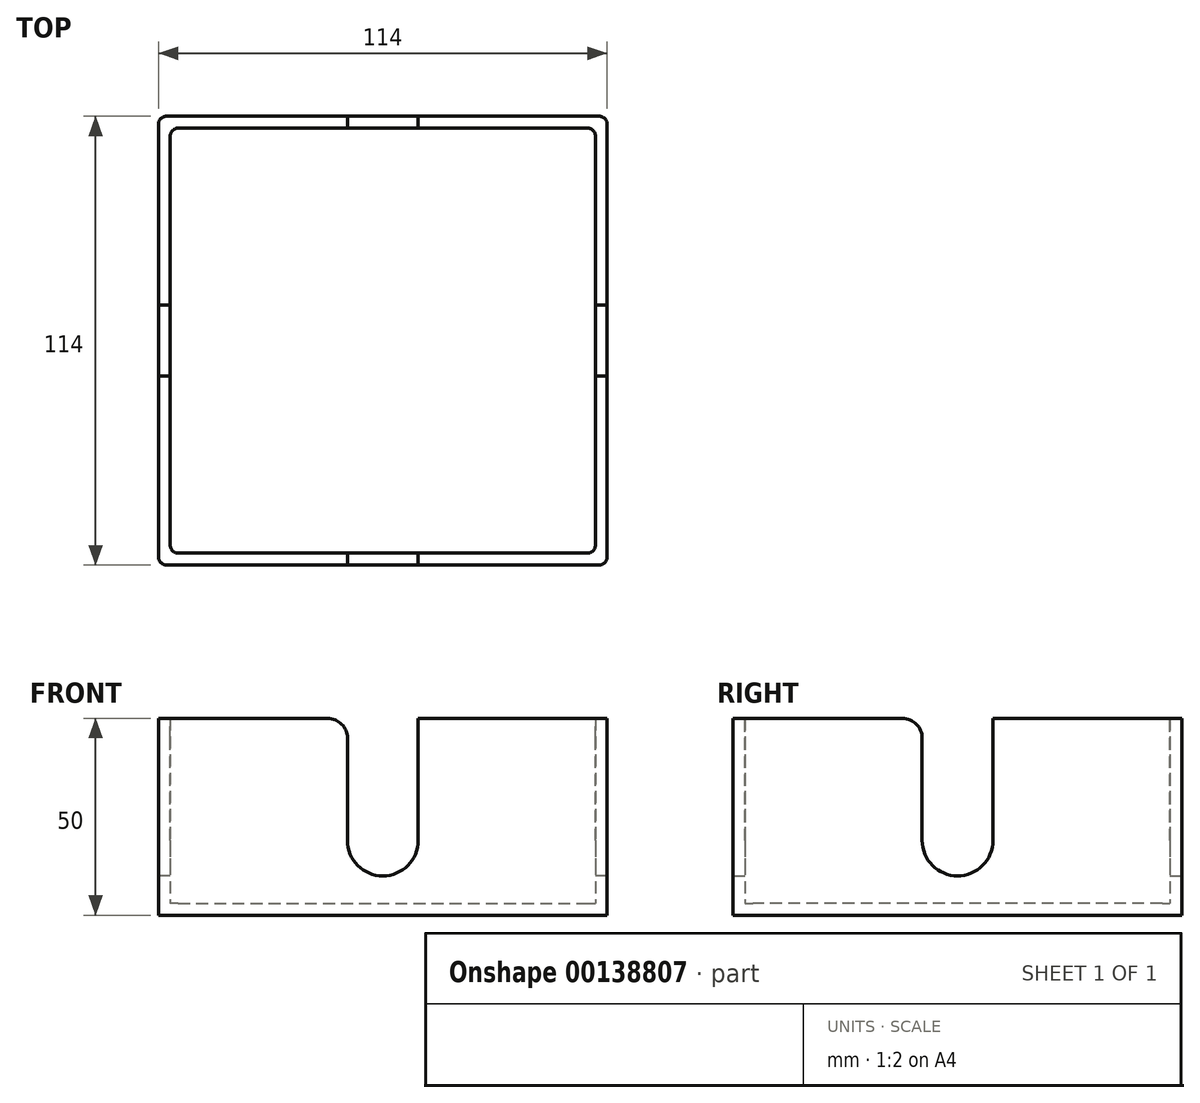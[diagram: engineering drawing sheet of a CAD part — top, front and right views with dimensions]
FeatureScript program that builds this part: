
annotation { "Feature Type Name" : "Feature", "Feature Type Description" : "" }
export const myFeature = defineFeature(function(context is Context, id is Id, definition is map)
    precondition{}
    {
        {
            var Q0;
            Q0=qCreatedBy(makeId("Top.planeOp"),FACE);
            var sketch = newSketch(context, id + "F0", { "sketchPlane" : qUnion([Q0])});
            skLineSegment(sketch, "E0.bottom", {"start": v(-32.98, 78.58) * mm, "end": v(81.02, 78.58) * mm});
            skLineSegment(sketch, "E0.top", {"start": v(-32.98, -35.42) * mm, "end": v(81.02, -35.42) * mm});
            skLineSegment(sketch, "E0.left", {"start": v(-32.98, 78.58) * mm, "end": v(-32.98, -35.42) * mm});
            skLineSegment(sketch, "E0.right", {"start": v(81.02, 78.58) * mm, "end": v(81.02, -35.42) * mm});
            skSolve(sketch);
        }
        {
            var Q0;
            Q0=makeQuery(id+"F0.imprint","IMPRINT",FACE,{"disambiguationData":[TD([[makeQuery(id+"F0.imprint","IMPRINT",EDGE,{"derivedFrom":sQuery(id+"F0.wireOp",EDGE,"E0.bottom")}),-1.0]])]});
            extrude(context, id + "F1", {"entities" : qUnion([Q0]), "depth" : 50 * mm});
        }
        {
            var Q0;
            Q0=makeQuery(id+"F1.opExtrude","CAP_FACE",FACE,{"disambiguationData":[OSD([sQuery(id+"F0.wireOp",EDGE,"E0.bottom"),sQuery(id+"F0.wireOp",EDGE,"E0.top"),sQuery(id+"F0.wireOp",EDGE,"E0.left"),sQuery(id+"F0.wireOp",EDGE,"E0.right")])],"isStart":false});
            shell(context, id + "F2", {"entities" : qUnion([Q0]), "thickness" : 3 * mm});
        }
        {
            var Q0;
            Q0=makeQuery(id+"F1.opExtrude","SWEPT_FACE",FACE,{"disambiguationData":[OSD([sQuery(id+"F0.wireOp",EDGE,"E0.left")])]});
            var sketch = newSketch(context, id + "F3", { "sketchPlane" : qUnion([Q0])});
            skLineSegment(sketch, "E1", {"start": v(-12.58, 62.87) * mm, "end": v(-12.58, 19) * mm});
            skArc(sketch, "E2", {"start": v(-30.58, 19) * mm, "mid": v(-21.58, 10) * mm, "end": v(-12.58, 19) * mm});
            skLineSegment(sketch, "E3", {"start": v(-30.58, 19) * mm, "end": v(-30.58, 62.87) * mm});
            skLineSegment(sketch, "E4", {"start": v(-30.58, 62.87) * mm, "end": v(-12.58, 62.87) * mm});
            skSolve(sketch);
        }
        {
            var Q0;
            {var subQ0=sQuery(id+"F3.wireOp",EDGE,"E2");Q0=makeQuery(id+"F3.imprint","IMPRINT",FACE,{"disambiguationData":[TD([[makeQuery(id+"F3.imprint","IMPRINT",EDGE,{"derivedFrom":subQ0}),1.0]])]});}
            extrude(context, id + "F4", {"entities" : qUnion([Q0]), "operationType" : NewBodyOperationType.REMOVE, "endBound" : BoundingType.THROUGH_ALL, "oppositeDirection" : true, "depth" : 165.16 * mm});
        }
        {
            var Q0;
            Q0=makeQuery(id+"F1.opExtrude","SWEPT_FACE",FACE,{"disambiguationData":[OSD([sQuery(id+"F0.wireOp",EDGE,"E0.bottom")])]});
            var sketch = newSketch(context, id + "F5", { "sketchPlane" : qUnion([Q0])});
            skLineSegment(sketch, "E5", {"start": v(-33.02, 19) * mm, "end": v(-33.02, 60.23) * mm});
            skLineSegment(sketch, "E6", {"start": v(-33.02, 60.23) * mm, "end": v(-15.02, 60.23) * mm});
            skLineSegment(sketch, "E7", {"start": v(-15.02, 60.23) * mm, "end": v(-15.02, 19) * mm});
            skArc(sketch, "E8", {"start": v(-33.02, 19) * mm, "mid": v(-24.02, 10) * mm, "end": v(-15.02, 19) * mm});
            skSolve(sketch);
        }
        {
            var Q0;
            {var subQ0=sQuery(id+"F5.wireOp",EDGE,"E8");Q0=makeQuery(id+"F5.imprint","IMPRINT",FACE,{"disambiguationData":[TD([[makeQuery(id+"F5.imprint","IMPRINT",EDGE,{"derivedFrom":subQ0}),1.0]])]});}
            extrude(context, id + "F6", {"entities" : qUnion([Q0]), "operationType" : NewBodyOperationType.REMOVE, "endBound" : BoundingType.THROUGH_ALL, "oppositeDirection" : true, "depth" : 25 * mm});
        }
        {
            var Q0;
            Q0=makeQuery(id+"F6.boolean.opBoolean","COPY",EDGE,{"disambiguationData":[OD(1.0)],"derivedFrom":makeQuery(id+"F6.opExtrude","SWEPT_EDGE",EDGE,{"disambiguationData":[OSD([sQuery(id+"F0.wireOp",EDGE,"E0.bottom"),sQuery(id+"F5.wireOp",EDGE,"E7")])]})});
            var Q1;
            Q1=makeQuery(id+"F6.boolean.opBoolean","COPY",EDGE,{"disambiguationData":[OD(1.0)],"derivedFrom":makeQuery(id+"F6.opExtrude","SWEPT_EDGE",EDGE,{"disambiguationData":[OSD([sQuery(id+"F0.wireOp",EDGE,"E0.bottom"),sQuery(id+"F5.wireOp",EDGE,"E5")])]})});
            var Q2;
            Q2=makeQuery(id+"F4.boolean.opBoolean","COPY",EDGE,{"disambiguationData":[OD(0.0)],"derivedFrom":makeQuery(id+"F4.opExtrude","SWEPT_EDGE",EDGE,{"disambiguationData":[OSD([sQuery(id+"F0.wireOp",EDGE,"E0.left"),sQuery(id+"F3.wireOp",EDGE,"E1")])]})});
            var Q3;
            Q3=makeQuery(id+"F4.boolean.opBoolean","COPY",EDGE,{"disambiguationData":[OD(0.0)],"derivedFrom":makeQuery(id+"F4.opExtrude","SWEPT_EDGE",EDGE,{"disambiguationData":[OSD([sQuery(id+"F0.wireOp",EDGE,"E0.left"),sQuery(id+"F3.wireOp",EDGE,"E3")])]})});
            var Q4;
            Q4=makeQuery(id+"F6.boolean.opBoolean","COPY",EDGE,{"disambiguationData":[OD(0.0)],"derivedFrom":makeQuery(id+"F6.opExtrude","SWEPT_EDGE",EDGE,{"disambiguationData":[OSD([sQuery(id+"F0.wireOp",EDGE,"E0.bottom"),sQuery(id+"F5.wireOp",EDGE,"E7")])]})});
            var Q5;
            Q5=makeQuery(id+"F6.boolean.opBoolean","COPY",EDGE,{"disambiguationData":[OD(0.0)],"derivedFrom":makeQuery(id+"F6.opExtrude","SWEPT_EDGE",EDGE,{"disambiguationData":[OSD([sQuery(id+"F0.wireOp",EDGE,"E0.bottom"),sQuery(id+"F5.wireOp",EDGE,"E5")])]})});
            var Q6;
            Q6=makeQuery(id+"F4.boolean.opBoolean","COPY",EDGE,{"disambiguationData":[OD(1.0)],"derivedFrom":makeQuery(id+"F4.opExtrude","SWEPT_EDGE",EDGE,{"disambiguationData":[OSD([sQuery(id+"F0.wireOp",EDGE,"E0.left"),sQuery(id+"F3.wireOp",EDGE,"E3")])]})});
            var Q7;
            Q7=makeQuery(id+"F4.boolean.opBoolean","COPY",EDGE,{"disambiguationData":[OD(1.0)],"derivedFrom":makeQuery(id+"F4.opExtrude","SWEPT_EDGE",EDGE,{"disambiguationData":[OSD([sQuery(id+"F0.wireOp",EDGE,"E0.left"),sQuery(id+"F3.wireOp",EDGE,"E1")])]})});
            fillet(context, id + "F7", {"entities" : qUnion([Q0, Q1, Q2, Q3, Q4, Q5, Q6, Q7]), "radius" : 5 * mm, "tangentPropagation" : true, "allowEdgeOverflow" : false});
        }
        {
            var Q0;
            Q0=makeQuery(id+"F1.opExtrude","SWEPT_EDGE",EDGE,{"disambiguationData":[OSD([sQuery(id+"F0.wireOp",EDGE,"E0.top"),sQuery(id+"F0.wireOp",EDGE,"E0.right")])]});
            var Q1;
            Q1=makeQuery(id+"F1.opExtrude","SWEPT_EDGE",EDGE,{"disambiguationData":[OSD([sQuery(id+"F0.wireOp",EDGE,"E0.top"),sQuery(id+"F0.wireOp",EDGE,"E0.left")])]});
            var Q2;
            Q2=makeQuery(id+"F1.opExtrude","SWEPT_EDGE",EDGE,{"disambiguationData":[OSD([sQuery(id+"F0.wireOp",EDGE,"E0.bottom"),sQuery(id+"F0.wireOp",EDGE,"E0.left")])]});
            var Q3;
            Q3=makeQuery(id+"F1.opExtrude","SWEPT_EDGE",EDGE,{"disambiguationData":[OSD([sQuery(id+"F0.wireOp",EDGE,"E0.bottom"),sQuery(id+"F0.wireOp",EDGE,"E0.right")])]});
            fillet(context, id + "F8", {"entities" : qUnion([Q0, Q1, Q2, Q3]), "radius" : 2 * mm, "tangentPropagation" : true, "allowEdgeOverflow" : false});
        }
        {
            var Q0;
            Q0=makeQuery(id+"F2.opShell","OFFSET_EDGE",EDGE,{"disambiguationData":[OSD([sQuery(id+"F0.wireOp",EDGE,"E0.top"),sQuery(id+"F0.wireOp",EDGE,"E0.left")])]});
            var Q1;
            Q1=makeQuery(id+"F2.opShell","OFFSET_EDGE",EDGE,{"disambiguationData":[OSD([sQuery(id+"F0.wireOp",EDGE,"E0.bottom"),sQuery(id+"F0.wireOp",EDGE,"E0.left")])]});
            var Q2;
            Q2=makeQuery(id+"F2.opShell","OFFSET_EDGE",EDGE,{"disambiguationData":[OSD([sQuery(id+"F0.wireOp",EDGE,"E0.bottom"),sQuery(id+"F0.wireOp",EDGE,"E0.right")])]});
            var Q3;
            Q3=makeQuery(id+"F2.opShell","OFFSET_EDGE",EDGE,{"disambiguationData":[OSD([sQuery(id+"F0.wireOp",EDGE,"E0.top"),sQuery(id+"F0.wireOp",EDGE,"E0.right")])]});
            fillet(context, id + "F9", {"entities" : qUnion([Q0, Q1, Q2, Q3]), "radius" : 2 * mm, "tangentPropagation" : true, "allowEdgeOverflow" : false});
        }
    });
